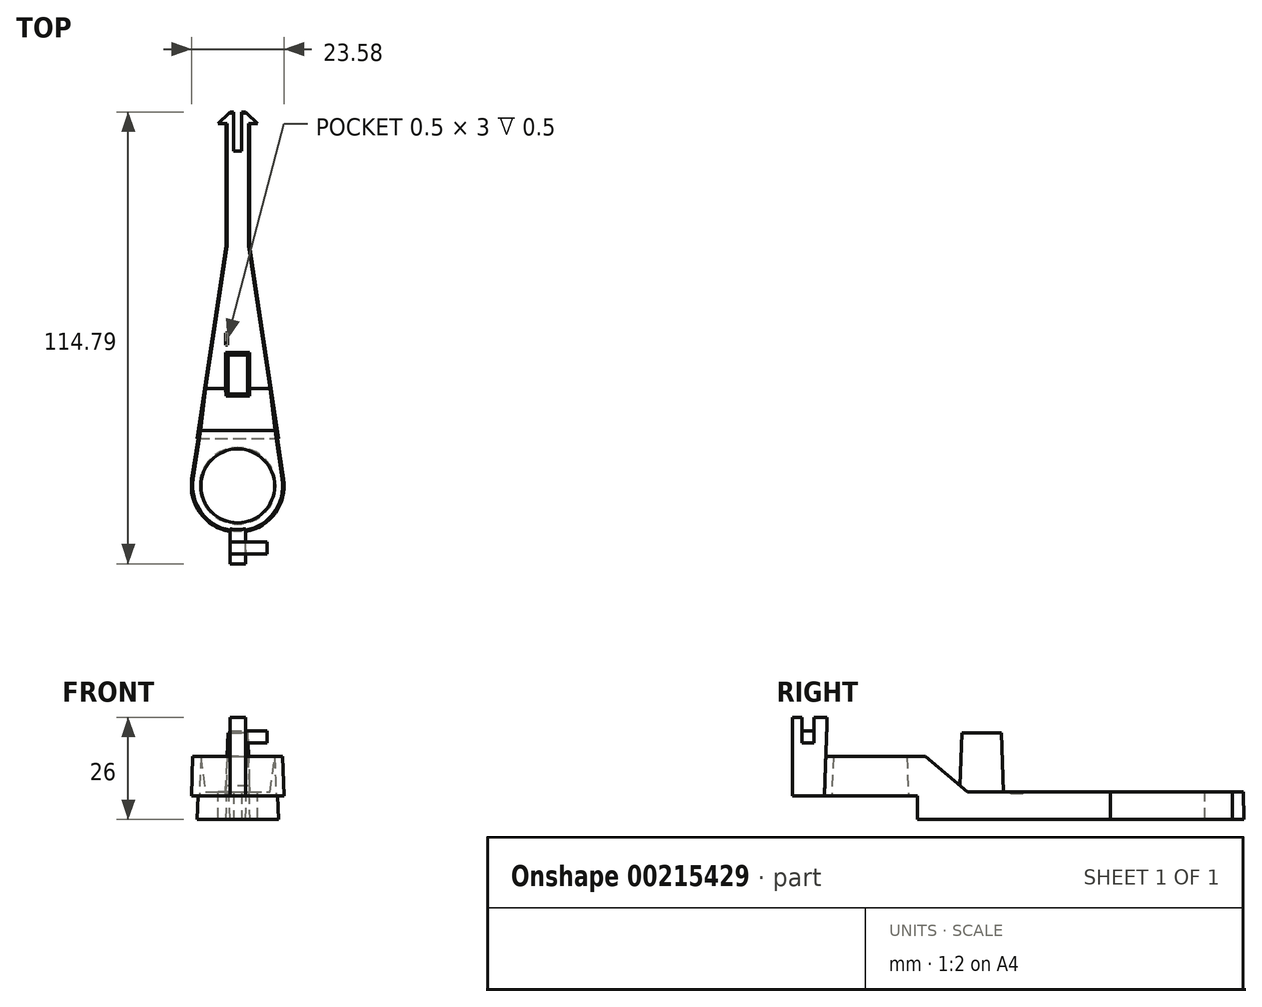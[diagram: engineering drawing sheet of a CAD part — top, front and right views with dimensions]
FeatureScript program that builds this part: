
annotation { "Feature Type Name" : "Feature", "Feature Type Description" : "" }
export const myFeature = defineFeature(function(context is Context, id is Id, definition is map)
    precondition{}
    {
        {
            var Q0;
            Q0=qCreatedBy(makeId("Top.planeOp"),FACE);
            var sketch = newSketch(context, id + "F0", { "sketchPlane" : qUnion([Q0])});
            skCircle(sketch, "E0", {"center": v(0, 0) * mm, "radius": 12 * mm});
            skLineSegment(sketch, "E1", {"start": v(-3, 95) * mm, "end": v(3, 95) * mm});
            skLineSegment(sketch, "E2", {"start": v(0, -12) * mm, "end": v(0, 95) * mm, "construction": true});
            skPoint(sketch, "E3", {"position": v(0, 95) * mm});
            skLineSegment(sketch, "E4", {"start": v(-3, 95) * mm, "end": v(-3, 61) * mm});
            skLineSegment(sketch, "E5", {"start": v(3, 95) * mm, "end": v(3, 61) * mm});
            skLineSegment(sketch, "E6", {"start": v(-3, 61) * mm, "end": v(-11.87, 1.78) * mm});
            skLineSegment(sketch, "E7", {"start": v(3, 61) * mm, "end": v(11.87, 1.78) * mm});
            skSolve(sketch);
        }
        {
            var Q0;
            Q0=qSketchRegion(id+"F0",true);
            extrude(context, id + "F1", {"entities" : qUnion([Q0]), "depth" : 16 * mm, "hasDraft" : true, "draftAngle" : 2 * degree, "draftPullDirection" : true});
        }
        {
            var Q0;
            Q0=qCreatedBy(makeId("Right.planeOp"),FACE);
            cPlane(context, id + "F2", {"entities" : qUnion([Q0]), "cplaneType" : CPlaneType.OFFSET, "offset" : 12 * mm, "width" : 150 * mm, "height" : 150 * mm});
        }
        {
            var Q0;
            Q0=qCreatedBy(id+"F2.planeOp",FACE);
            var sketch = newSketch(context, id + "F3", { "sketchPlane" : qUnion([Q0])});
            skLineSegment(sketch, "E8", {"start": v(94.76, 7) * mm, "end": v(24.76, 7) * mm});
            skLineSegment(sketch, "E9", {"start": v(24.76, 7) * mm, "end": v(14.03, 16) * mm});
            skLineSegment(sketch, "E10", {"start": v(12, 0) * mm, "end": v(12, 6) * mm});
            skLineSegment(sketch, "E11", {"start": v(12, 6) * mm, "end": v(-11.8, 6) * mm});
            skLineSegment(sketch, "E12", {"start": v(12, 0) * mm, "end": v(-12, 0) * mm});
            skLineSegment(sketch, "E13", {"start": v(-12, 0) * mm, "end": v(-11.8, 6) * mm});
            skLineSegment(sketch, "E14", {"start": v(14.03, 16) * mm, "end": v(94.44, 16) * mm});
            skLineSegment(sketch, "E15", {"start": v(94.44, 16) * mm, "end": v(94.76, 7) * mm});
            skSolve(sketch);
        }
        {
            var Q0;
            Q0=qSketchRegion(id+"F3",true);
            extrude(context, id + "F4", {"entities" : qUnion([Q0]), "operationType" : NewBodyOperationType.REMOVE, "endBound" : BoundingType.THROUGH_ALL, "oppositeDirection" : true, "depth" : 25 * mm});
        }
        {
            var Q0;
            Q0=makeQuery(id+"F4.boolean.opBoolean","COPY",FACE,{"derivedFrom":makeQuery(id+"F4.opExtrude","SWEPT_FACE",FACE,{"disambiguationData":[OSD([sQuery(id+"F3.wireOp",EDGE,"E8")])]})});
            cPlane(context, id + "F5", {"entities" : qUnion([Q0]), "cplaneType" : CPlaneType.OFFSET, "offset" : 15 * mm, "width" : 150 * mm, "height" : 150 * mm});
        }
        {
            var Q0;
            Q0=qCreatedBy(id+"F5.planeOp",FACE);
            var sketch = newSketch(context, id + "F6", { "sketchPlane" : qUnion([Q0])});
            skLineSegment(sketch, "E16.bottom", {"start": v(-2.5, 23.3) * mm, "end": v(2.5, 23.3) * mm});
            skLineSegment(sketch, "E16.top", {"start": v(-2.5, 33.3) * mm, "end": v(2.5, 33.3) * mm});
            skLineSegment(sketch, "E16.left", {"start": v(-2.5, 23.3) * mm, "end": v(-2.5, 33.3) * mm});
            skLineSegment(sketch, "E16.right", {"start": v(2.5, 23.3) * mm, "end": v(2.5, 33.3) * mm});
            skPoint(sketch, "E16.middle", {"position": v(0, 28.3) * mm});
            skSolve(sketch);
        }
        {
            var Q0;
            Q0=qSketchRegion(id+"F6",true);
            extrude(context, id + "F7", {"entities" : qUnion([Q0]), "operationType" : NewBodyOperationType.ADD, "endBound" : BoundingType.UP_TO_NEXT, "oppositeDirection" : true, "depth" : 25 * mm, "hasDraft" : true, "draftAngle" : 2 * degree});
        }
        {
            var Q0;
            Q0=makeQuery(id+"F4.boolean.opBoolean","COPY",FACE,{"derivedFrom":makeQuery(id+"F4.opExtrude","SWEPT_FACE",FACE,{"disambiguationData":[OSD([sQuery(id+"F3.wireOp",EDGE,"E11")])]})});
            var sketch = newSketch(context, id + "F8", { "sketchPlane" : qUnion([Q0])});
            skCircle(sketch, "E17", {"center": v(0, 0) * mm, "radius": 9.72 * mm});
            skSolve(sketch);
        }
        {
            var Q0;
            Q0=qSketchRegion(id+"F8",true);
            extrude(context, id + "F9", {"entities" : qUnion([Q0]), "operationType" : NewBodyOperationType.REMOVE, "endBound" : BoundingType.THROUGH_ALL, "oppositeDirection" : true, "depth" : 25 * mm, "hasDraft" : true, "draftAngle" : 2 * degree, "draftPullDirection" : true});
        }
        {
            var Q0;
            Q0=makeQuery(id+"F4.boolean.opBoolean","COPY",FACE,{"derivedFrom":makeQuery(id+"F4.opExtrude","SWEPT_FACE",FACE,{"disambiguationData":[OSD([sQuery(id+"F3.wireOp",EDGE,"E11")])]})});
            var sketch = newSketch(context, id + "F10", { "sketchPlane" : qUnion([Q0])});
            skLineSegment(sketch, "E18", {"start": v(0, 11.8) * mm, "end": v(0, 19.8) * mm, "construction": true});
            skPoint(sketch, "E18.endSnap0", {"position": v(0, 11.8) * mm});
            skLineSegment(sketch, "E19", {"start": v(0, 19.8) * mm, "end": v(-2, 19.8) * mm});
            skLineSegment(sketch, "E20", {"start": v(-2, 19.8) * mm, "end": v(-2, 11.62) * mm});
            skLineSegment(sketch, "E21", {"start": v(0, 19.8) * mm, "end": v(2, 19.8) * mm});
            skLineSegment(sketch, "E22", {"start": v(2, 19.8) * mm, "end": v(2, 11.62) * mm});
            skArc(sketch, "E23", {"start": v(2, 11.62) * mm, "mid": v(0, 11.8) * mm, "end": v(-2, 11.62) * mm});
            skSolve(sketch);
        }
        {
            var Q0;
            Q0=qCreatedBy(makeId("Front.planeOp"),FACE);
            var Q1;
            Q1=sQuery(id+"F10.wireOp",VERTEX,"E21.start");
            cPlane(context, id + "F11", {"entities" : qUnion([Q0, Q1]), "cplaneType" : CPlaneType.PLANE_POINT, "offset" : 25 * mm, "width" : 150 * mm, "height" : 150 * mm});
        }
        {
            var Q0;
            Q0=qCreatedBy(id+"F11.planeOp",FACE);
            var sketch = newSketch(context, id + "F12", { "sketchPlane" : qUnion([Q0])});
            skLineSegment(sketch, "E24.bottom", {"start": v(-2, 6) * mm, "end": v(2, 6) * mm});
            skLineSegment(sketch, "E24.top", {"start": v(-2, 26) * mm, "end": v(2, 26) * mm});
            skLineSegment(sketch, "E24.left", {"start": v(-2, 6) * mm, "end": v(-2, 26) * mm});
            skLineSegment(sketch, "E24.right", {"start": v(2, 6) * mm, "end": v(2, 26) * mm});
            skSolve(sketch);
        }
        {
            var Q0;
            Q0=qSketchRegion(id+"F12",true);
            var Q1;
            Q1=makeQuery(id+"F1.opExtrude","SWEPT_FACE",FACE,{"disambiguationData":[OSD([sQuery(id+"F0.wireOp",EDGE,"E0")])]});
            extrude(context, id + "F13", {"entities" : qUnion([Q0]), "operationType" : NewBodyOperationType.ADD, "endBound" : BoundingType.UP_TO_SURFACE, "oppositeDirection" : true, "endBoundEntityFace" : qUnion([Q1]), "depth" : 8 * mm});
        }
        {
            var Q0;
            Q0=makeQuery(id+"F13.opExtrude","SWEPT_FACE",FACE,{"disambiguationData":[OSD([sQuery(id+"F12.wireOp",EDGE,"E24.right")])]});
            var sketch = newSketch(context, id + "F14", { "sketchPlane" : qUnion([Q0])});
            skLineSegment(sketch, "E25.bottom", {"start": v(-17.3, 22.5) * mm, "end": v(-14.3, 22.5) * mm});
            skLineSegment(sketch, "E25.top", {"start": v(-17.3, 19.5) * mm, "end": v(-14.3, 19.5) * mm});
            skLineSegment(sketch, "E25.left", {"start": v(-17.3, 22.5) * mm, "end": v(-17.3, 19.5) * mm});
            skLineSegment(sketch, "E25.right", {"start": v(-14.3, 22.5) * mm, "end": v(-14.3, 19.5) * mm});
            skSolve(sketch);
        }
        {
            var Q0;
            Q0=qSketchRegion(id+"F14",true);
            extrude(context, id + "F15", {"entities" : qUnion([Q0]), "operationType" : NewBodyOperationType.ADD, "depth" : 5.5 * mm});
        }
        {
            var Q0;
            Q0=makeQuery(id+"F13.opExtrude","SWEPT_FACE",FACE,{"disambiguationData":[OSD([sQuery(id+"F12.wireOp",EDGE,"E24.right")])]});
            var sketch = newSketch(context, id + "F16", { "sketchPlane" : qUnion([Q0])});
            skLineSegment(sketch, "E26.bottom", {"start": v(-17.3, 22.5) * mm, "end": v(-14.3, 22.5) * mm});
            skLineSegment(sketch, "E26.top", {"start": v(-17.3, 26) * mm, "end": v(-14.3, 26) * mm});
            skLineSegment(sketch, "E26.left", {"start": v(-17.3, 22.5) * mm, "end": v(-17.3, 26) * mm});
            skLineSegment(sketch, "E26.right", {"start": v(-14.3, 22.5) * mm, "end": v(-14.3, 26) * mm});
            skSolve(sketch);
        }
        {
            var Q0;
            Q0=qSketchRegion(id+"F16",true);
            extrude(context, id + "F17", {"entities" : qUnion([Q0]), "operationType" : NewBodyOperationType.REMOVE, "endBound" : BoundingType.THROUGH_ALL, "oppositeDirection" : true, "depth" : 25 * mm});
        }
        {
            var Q0;
            Q0=makeQuery(id+"F4.boolean.opBoolean","COPY",FACE,{"derivedFrom":makeQuery(id+"F4.opExtrude","SWEPT_FACE",FACE,{"disambiguationData":[OSD([sQuery(id+"F3.wireOp",EDGE,"E8")])]})});
            var sketch = newSketch(context, id + "F18", { "sketchPlane" : qUnion([Q0])});
            skLineSegment(sketch, "E27.bottom", {"start": v(-3.02, 38.82) * mm, "end": v(-2.52, 38.82) * mm});
            skLineSegment(sketch, "E27.top", {"start": v(-3.02, 35.82) * mm, "end": v(-2.52, 35.82) * mm});
            skLineSegment(sketch, "E27.left", {"start": v(-3.02, 38.82) * mm, "end": v(-3.02, 35.82) * mm});
            skLineSegment(sketch, "E27.right", {"start": v(-2.52, 38.82) * mm, "end": v(-2.52, 35.82) * mm});
            skSolve(sketch);
        }
        {
            var Q0;
            Q0=qSketchRegion(id+"F18",true);
            extrude(context, id + "F19", {"entities" : qUnion([Q0]), "operationType" : NewBodyOperationType.REMOVE, "oppositeDirection" : true, "depth" : 0.5 * mm});
        }
        {
            var Q0;
            Q0=makeQuery(id+"F4.boolean.opBoolean","COPY",FACE,{"derivedFrom":makeQuery(id+"F4.opExtrude","SWEPT_FACE",FACE,{"disambiguationData":[OSD([sQuery(id+"F3.wireOp",EDGE,"E8")])]})});
            var sketch = newSketch(context, id + "F20", { "sketchPlane" : qUnion([Q0])});
            skLineSegment(sketch, "E28", {"start": v(0, 95) * mm, "end": v(0, 85) * mm});
            skLineSegment(sketch, "E29", {"start": v(0, 85) * mm, "end": v(-1, 85) * mm});
            skLineSegment(sketch, "E30", {"start": v(-1, 85) * mm, "end": v(-1, 95) * mm});
            skLineSegment(sketch, "E31", {"start": v(-1, 95) * mm, "end": v(-2, 95) * mm});
            skLineSegment(sketch, "E32", {"start": v(-2, 95) * mm, "end": v(-5, 92) * mm});
            skLineSegment(sketch, "E33", {"start": v(-2, 95) * mm, "end": v(-5, 95) * mm});
            skLineSegment(sketch, "E34", {"start": v(-5, 95) * mm, "end": v(-5, 92) * mm});
            skLineSegment(sketch, "E35", {"start": v(-3, 95) * mm, "end": v(-3, 90.83) * mm});
            skLineSegment(sketch, "E36", {"start": v(-5, 92) * mm, "end": v(-3, 92) * mm});
            skLineSegment(sketch, "E37", {"start": v(-1, 95) * mm, "end": v(0, 95) * mm});
            skLineSegment(sketch, "E38.MirrorCS", {"start": v(2, 95) * mm, "end": v(5, 95) * mm});
            skLineSegment(sketch, "E39.MirrorCS", {"start": v(1, 95) * mm, "end": v(2, 95) * mm});
            skLineSegment(sketch, "E40.MirrorCS", {"start": v(1, 95) * mm, "end": v(0, 95) * mm});
            skLineSegment(sketch, "E41.MirrorCS", {"start": v(1, 85) * mm, "end": v(1, 95) * mm});
            skLineSegment(sketch, "E42.MirrorCS", {"start": v(0, 85) * mm, "end": v(1, 85) * mm});
            skLineSegment(sketch, "E43.MirrorCS", {"start": v(5, 92) * mm, "end": v(3, 92) * mm});
            skLineSegment(sketch, "E44.MirrorCS", {"start": v(3, 95) * mm, "end": v(3, 90.83) * mm});
            skLineSegment(sketch, "E45.MirrorCS", {"start": v(2, 95) * mm, "end": v(5, 92) * mm});
            skLineSegment(sketch, "E46.MirrorCS", {"start": v(5, 95) * mm, "end": v(5, 92) * mm});
            skLineSegment(sketch, "E47", {"start": v(-2.76, 94.24) * mm, "end": v(-2.76, 92) * mm});
            skLineSegment(sketch, "E48", {"start": v(-2.76, 92) * mm, "end": v(-3, 92) * mm});
            skLineSegment(sketch, "E49.MirrorCS", {"start": v(2.76, 94.24) * mm, "end": v(2.76, 92) * mm});
            skLineSegment(sketch, "E50.MirrorCS", {"start": v(2.76, 92) * mm, "end": v(3, 92) * mm});
            skSolve(sketch);
        }
        {
            var Q0;
            {var subQ0=sQuery(id+"F20.wireOp",EDGE,"E35");var subQ1=sQuery(id+"F20.wireOp",EDGE,"E33");var subQ2=makeQuery(id+"F20.imprint","INTERSECT",VERTEX,{"derivedFrom":[subQ1,subQ0]});Q0=makeQuery(id+"F20.imprint","IMPRINT",FACE,{"disambiguationData":[TD([[makeQuery(id+"F20.imprint","IMPRINT",EDGE,{"disambiguationData":[TD([[subQ2,-1.0]])],"derivedFrom":subQ0}),1.0]])]});}
            var Q1;
            {var subQ0=sQuery(id+"F20.wireOp",EDGE,"E32");var subQ1=sQuery(id+"F3.wireOp",EDGE,"E8");var subQ2=makeQuery(id+"F4.boolean.opBoolean","INTERSECT",EDGE,{"derivedFrom":[makeQuery(id+"F1.opExtrude","SWEPT_FACE",FACE,{"disambiguationData":[OSD([sQuery(id+"F0.wireOp",EDGE,"E4")])]}),makeQuery(id+"F4.opExtrude","SWEPT_FACE",FACE,{"disambiguationData":[OSD([subQ1])]})]});var subQ3=makeQuery(id+"F20.imprint","INTERSECT",VERTEX,{"derivedFrom":[subQ2,subQ0]});Q1=makeQuery(id+"F20.imprint","IMPRINT",FACE,{"disambiguationData":[TD([[makeQuery(id+"F20.imprint","IMPRINT",EDGE,{"disambiguationData":[TD([[subQ3,1.0]])],"derivedFrom":subQ0}),-1.0]])]});}
            var Q2;
            {var subQ1=sQuery(id+"F20.wireOp",EDGE,"E44.MirrorCS");var subQ6=sQuery(id+"F20.wireOp",EDGE,"E38.MirrorCS");var subQ10=makeQuery(id+"F20.imprint","INTERSECT",VERTEX,{"derivedFrom":[subQ6,subQ1]});Q2=makeQuery(id+"F20.imprint","IMPRINT",FACE,{"disambiguationData":[TD([[makeQuery(id+"F20.imprint","IMPRINT",EDGE,{"disambiguationData":[TD([[subQ10,-1.0]])],"derivedFrom":subQ1}),-1.0]])]});}
            var Q3;
            {var subQ0=sQuery(id+"F20.wireOp",EDGE,"E45.MirrorCS");var subQ1=sQuery(id+"F3.wireOp",EDGE,"E8");var subQ2=makeQuery(id+"F4.boolean.opBoolean","INTERSECT",EDGE,{"derivedFrom":[makeQuery(id+"F1.opExtrude","SWEPT_FACE",FACE,{"disambiguationData":[OSD([sQuery(id+"F0.wireOp",EDGE,"E5")])]}),makeQuery(id+"F4.opExtrude","SWEPT_FACE",FACE,{"disambiguationData":[OSD([subQ1])]})]});var subQ3=makeQuery(id+"F20.imprint","INTERSECT",VERTEX,{"derivedFrom":[subQ2,subQ0]});Q3=makeQuery(id+"F20.imprint","IMPRINT",FACE,{"disambiguationData":[TD([[makeQuery(id+"F20.imprint","IMPRINT",EDGE,{"disambiguationData":[TD([[subQ3,1.0]])],"derivedFrom":subQ0}),1.0]])]});}
            var Q4;
            {var subQ0=sQuery(id+"F20.wireOp",EDGE,"E42.MirrorCS");Q4=makeQuery(id+"F20.imprint","IMPRINT",FACE,{"disambiguationData":[TD([[makeQuery(id+"F20.imprint","IMPRINT",EDGE,{"derivedFrom":subQ0}),1.0]])]});}
            var Q5;
            {var subQ0=sQuery(id+"F20.wireOp",EDGE,"E29");Q5=makeQuery(id+"F20.imprint","IMPRINT",FACE,{"disambiguationData":[TD([[makeQuery(id+"F20.imprint","IMPRINT",EDGE,{"derivedFrom":subQ0}),-1.0]])]});}
            var Q6;
            {var subQ0=sQuery(id+"F20.wireOp",EDGE,"E37");Q6=makeQuery(id+"F20.imprint","IMPRINT",FACE,{"disambiguationData":[TD([[makeQuery(id+"F20.imprint","IMPRINT",EDGE,{"derivedFrom":subQ0}),-1.0]])]});}
            var Q7;
            {var subQ0=sQuery(id+"F20.wireOp",EDGE,"E40.MirrorCS");Q7=makeQuery(id+"F20.imprint","IMPRINT",FACE,{"disambiguationData":[TD([[makeQuery(id+"F20.imprint","IMPRINT",EDGE,{"derivedFrom":subQ0}),1.0]])]});}
            extrude(context, id + "F21", {"entities" : qUnion([Q0, Q1, Q2, Q3, Q4, Q5, Q6, Q7]), "operationType" : NewBodyOperationType.REMOVE, "endBound" : BoundingType.THROUGH_ALL, "oppositeDirection" : true, "depth" : 25 * mm});
        }
        {
            var Q0;
            {var subQ0=sQuery(id+"F20.wireOp",EDGE,"E36");Q0=makeQuery(id+"F20.imprint","IMPRINT",FACE,{"disambiguationData":[TD([[makeQuery(id+"F20.imprint","IMPRINT",EDGE,{"derivedFrom":subQ0}),1.0]])]});}
            var Q1;
            {var subQ0=sQuery(id+"F20.wireOp",EDGE,"E47");Q1=makeQuery(id+"F20.imprint","IMPRINT",FACE,{"disambiguationData":[TD([[makeQuery(id+"F20.imprint","IMPRINT",EDGE,{"derivedFrom":subQ0}),-1.0]])]});}
            var Q2;
            {var subQ4=sQuery(id+"F20.wireOp",EDGE,"E49.MirrorCS");Q2=makeQuery(id+"F20.imprint","IMPRINT",FACE,{"disambiguationData":[TD([[makeQuery(id+"F20.imprint","IMPRINT",EDGE,{"derivedFrom":subQ4}),1.0]])]});}
            var Q3;
            {var subQ0=sQuery(id+"F20.wireOp",EDGE,"E43.MirrorCS");Q3=makeQuery(id+"F20.imprint","IMPRINT",FACE,{"disambiguationData":[TD([[makeQuery(id+"F20.imprint","IMPRINT",EDGE,{"derivedFrom":subQ0}),-1.0]])]});}
            var Q4;
            Q4=makeQuery(id+"F1.opExtrude","CAP_FACE",FACE,{"disambiguationData":[OSD([sQuery(id+"F0.wireOp",EDGE,"E0"),sQuery(id+"F0.wireOp",EDGE,"E1"),sQuery(id+"F0.wireOp",EDGE,"E4"),sQuery(id+"F0.wireOp",EDGE,"E5"),sQuery(id+"F0.wireOp",EDGE,"E6"),sQuery(id+"F0.wireOp",EDGE,"E7")])],"isStart":true});
            extrude(context, id + "F22", {"entities" : qUnion([Q0, Q1, Q2, Q3]), "operationType" : NewBodyOperationType.ADD, "endBound" : BoundingType.UP_TO_SURFACE, "oppositeDirection" : true, "endBoundEntityFace" : qUnion([Q4]), "depth" : 25 * mm});
        }
    });
